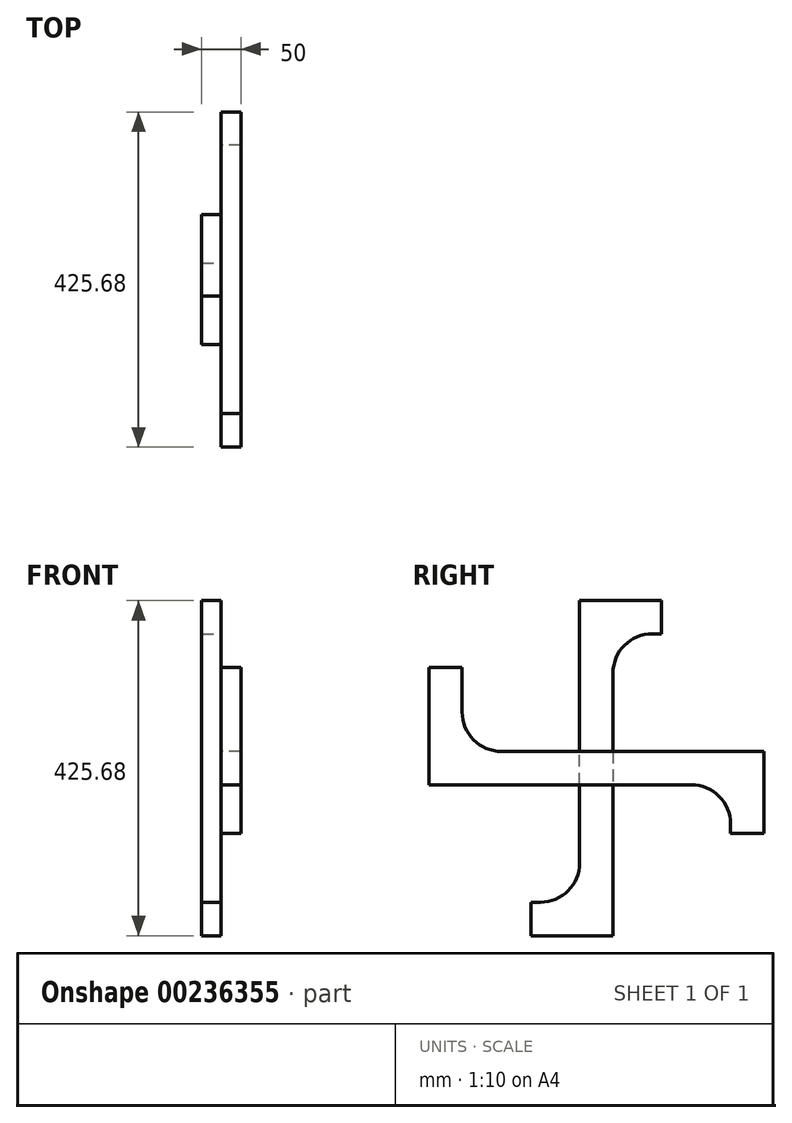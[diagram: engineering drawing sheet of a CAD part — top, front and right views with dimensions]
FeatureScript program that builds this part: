
annotation { "Feature Type Name" : "Feature", "Feature Type Description" : "" }
export const myFeature = defineFeature(function(context is Context, id is Id, definition is map)
    precondition{}
    {
        {
            var Q0;
            Q0=qCreatedBy(makeId("Right.planeOp"),FACE);
            var sketch = newSketch(context, id + "F0", { "sketchPlane" : qUnion([Q0])});
            skLineSegment(sketch, "E0", {"start": v(-21.14, 212.84) * mm, "end": v(21.14, 212.84) * mm});
            skLineSegment(sketch, "E1", {"start": v(21.14, 120.55) * mm, "end": v(21.14, 21.14) * mm});
            skLineSegment(sketch, "E2", {"start": v(21.14, -212.84) * mm, "end": v(-21.14, -212.84) * mm});
            skLineSegment(sketch, "E3", {"start": v(-21.14, -120.55) * mm, "end": v(-21.14, -21.14) * mm});
            skPoint(sketch, "E4", {"position": v(0, 0) * mm});
            skLineSegment(sketch, "E5", {"start": v(-120.55, 21.14) * mm, "end": v(-21.14, 21.14) * mm});
            skLineSegment(sketch, "E6", {"start": v(212.84, 21.14) * mm, "end": v(212.84, -21.14) * mm});
            skLineSegment(sketch, "E7", {"start": v(120.55, -21.14) * mm, "end": v(21.14, -21.14) * mm});
            skLineSegment(sketch, "E8", {"start": v(-212.84, -21.14) * mm, "end": v(-212.84, 21.14) * mm});
            skLineSegment(sketch, "E9", {"start": v(-21.14, -212.84) * mm, "end": v(-82.72, -212.84) * mm});
            skLineSegment(sketch, "E10", {"start": v(-82.72, -212.84) * mm, "end": v(-82.72, -170.55) * mm});
            skLineSegment(sketch, "E11", {"start": v(-82.72, -170.55) * mm, "end": v(-71.14, -170.55) * mm});
            skLineSegment(sketch, "E12", {"start": v(212.84, -21.14) * mm, "end": v(212.84, -82.72) * mm});
            skLineSegment(sketch, "E13", {"start": v(212.84, -82.72) * mm, "end": v(170.55, -82.72) * mm});
            skLineSegment(sketch, "E14", {"start": v(170.55, -82.72) * mm, "end": v(170.55, -71.14) * mm});
            skLineSegment(sketch, "E15", {"start": v(21.14, 212.84) * mm, "end": v(82.72, 212.84) * mm});
            skLineSegment(sketch, "E16", {"start": v(82.72, 212.84) * mm, "end": v(82.72, 170.55) * mm});
            skLineSegment(sketch, "E17", {"start": v(82.72, 170.55) * mm, "end": v(71.14, 170.55) * mm});
            skLineSegment(sketch, "E18", {"start": v(-212.84, 21.14) * mm, "end": v(-212.84, 127.72) * mm});
            skLineSegment(sketch, "E19", {"start": v(-212.84, 127.72) * mm, "end": v(-170.55, 127.72) * mm});
            skLineSegment(sketch, "E20", {"start": v(-170.55, 127.72) * mm, "end": v(-170.55, 71.14) * mm});
            skLineSegment(sketch, "E21.trimOffspring", {"start": v(-21.14, 21.14) * mm, "end": v(-21.14, 212.84) * mm});
            skLineSegment(sketch, "E22.trimOffspring", {"start": v(21.14, -21.14) * mm, "end": v(21.14, -212.84) * mm});
            skLineSegment(sketch, "E23.trimOffspring", {"start": v(-21.14, -21.14) * mm, "end": v(-212.84, -21.14) * mm});
            skLineSegment(sketch, "E24.trimOffspring", {"start": v(21.14, 21.14) * mm, "end": v(212.84, 21.14) * mm});
            skLineSegment(sketch, "E25", {"start": v(-21.14, 21.14) * mm, "end": v(-21.14, -21.14) * mm});
            skLineSegment(sketch, "E26", {"start": v(21.14, -21.14) * mm, "end": v(-21.14, -21.14) * mm});
            skLineSegment(sketch, "E27", {"start": v(21.14, 21.14) * mm, "end": v(21.14, -21.14) * mm});
            skLineSegment(sketch, "E28", {"start": v(-21.14, 21.14) * mm, "end": v(21.14, 21.14) * mm});
            skPoint(sketch, "E29.visualSharp", {"position": v(-170.55, 21.14) * mm});
            skArc(sketch, "E29.filletArc", {"start": v(-170.55, 71.14) * mm, "mid": v(-155.91, 35.79) * mm, "end": v(-120.55, 21.14) * mm});
            skPoint(sketch, "E30.visualSharp", {"position": v(170.55, -21.14) * mm});
            skArc(sketch, "E30.filletArc", {"start": v(170.55, -71.14) * mm, "mid": v(155.91, -35.79) * mm, "end": v(120.55, -21.14) * mm});
            skPoint(sketch, "E31.visualSharp", {"position": v(-21.14, -170.55) * mm});
            skArc(sketch, "E31.filletArc", {"start": v(-71.14, -170.55) * mm, "mid": v(-35.79, -155.91) * mm, "end": v(-21.14, -120.55) * mm});
            skPoint(sketch, "E32.visualSharp", {"position": v(21.14, 170.55) * mm});
            skArc(sketch, "E32.filletArc", {"start": v(71.14, 170.55) * mm, "mid": v(35.79, 155.91) * mm, "end": v(21.14, 120.55) * mm});
            skSolve(sketch);
        }
        {
            var Q0;
            Q0=makeQuery(id+"F0.imprint","IMPRINT",FACE,{"disambiguationData":[TD([[makeQuery(id+"F0.imprint","IMPRINT",EDGE,{"derivedFrom":sQuery(id+"F0.wireOp",EDGE,"E5")}),-1.0]])]});
            var Q1;
            Q1=makeQuery(id+"F0.imprint","IMPRINT",FACE,{"disambiguationData":[TD([[makeQuery(id+"F0.imprint","IMPRINT",EDGE,{"derivedFrom":sQuery(id+"F0.wireOp",EDGE,"E6")}),-1.0]])]});
            var Q2;
            Q2=makeQuery(id+"F0.imprint","IMPRINT",FACE,{"disambiguationData":[TD([[makeQuery(id+"F0.imprint","IMPRINT",EDGE,{"derivedFrom":sQuery(id+"F0.wireOp",EDGE,"E25")}),1.0]])]});
            extrude(context, id + "F1", {"entities" : qUnion([Q0, Q1, Q2]), "depth" : 25 * mm});
        }
        {
            var Q0;
            Q0=makeQuery(id+"F0.imprint","IMPRINT",FACE,{"disambiguationData":[TD([[makeQuery(id+"F0.imprint","IMPRINT",EDGE,{"derivedFrom":sQuery(id+"F0.wireOp",EDGE,"E2")}),-1.0]])]});
            var Q1;
            Q1=makeQuery(id+"F0.imprint","IMPRINT",FACE,{"disambiguationData":[TD([[makeQuery(id+"F0.imprint","IMPRINT",EDGE,{"derivedFrom":sQuery(id+"F0.wireOp",EDGE,"E25")}),1.0]])]});
            var Q2;
            Q2=makeQuery(id+"F0.imprint","IMPRINT",FACE,{"disambiguationData":[TD([[makeQuery(id+"F0.imprint","IMPRINT",EDGE,{"derivedFrom":sQuery(id+"F0.wireOp",EDGE,"E0")}),-1.0]])]});
            extrude(context, id + "F2", {"entities" : qUnion([Q0, Q1, Q2]), "oppositeDirection" : true, "depth" : 25 * mm});
        }
    });
